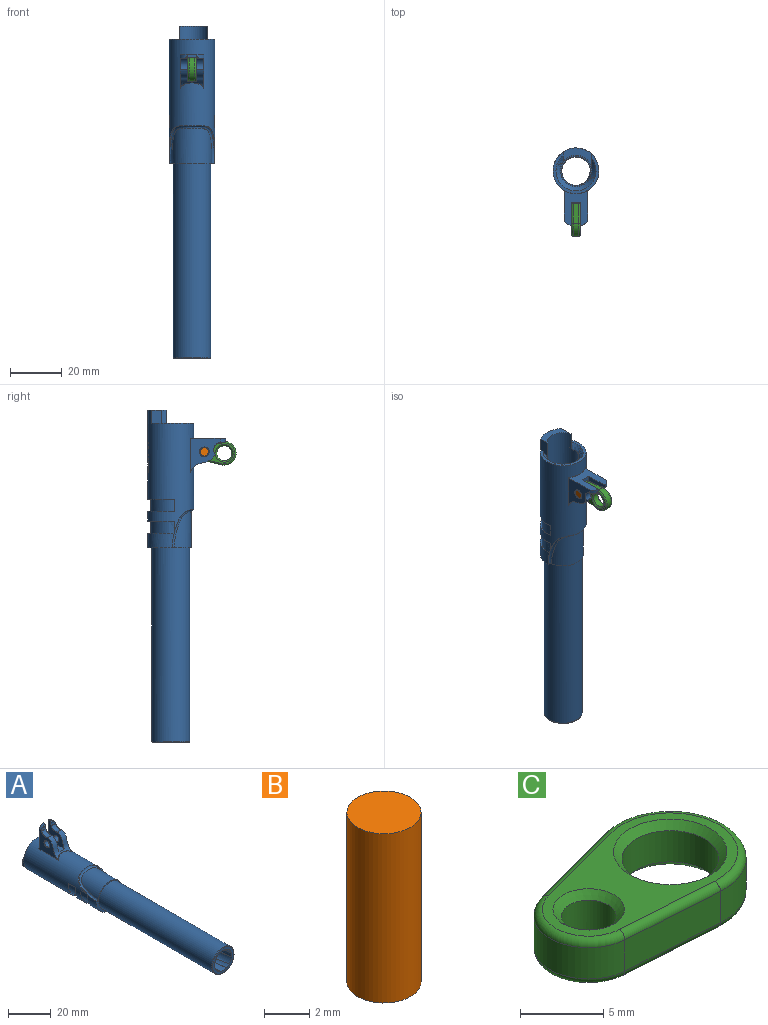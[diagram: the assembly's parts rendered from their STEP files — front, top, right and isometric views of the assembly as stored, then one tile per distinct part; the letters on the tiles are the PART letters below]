
ASSEMBLY  parts=3 mates=2
PART A: 333 faces, bbox 31.5x130.4x32.7 mm
  f0: bspline ~95.71x9.97mm, area 220mm2, adj f16,f17,f18,f23
  f1: bspline ~95.71x9.42mm, area 220mm2, adj f14,f15,f22,f23
  f2: bspline ~95.71x9.97mm, area 220mm2, adj f11,f12,f13,f23
  f3: bspline ~95.71x11mm, area 220mm2, adj f8,f9,f10,f23
  f4: bspline ~95.71x9.42mm, area 220mm2, adj f19,f20,f21,f23
  f5: bspline ~95.71x11mm, area 220mm2, adj f23,f24,f25,f26
  f6: bspline ~14.67x14.67mm, area 9.1mm2, adj f7,f23,f39
  f7: bspline ~14.67x14.67mm, area 9.1mm2, adj f6,f23,f39
  f8: bspline ~95.71x9.97mm, area 14.2mm2, adj f3,f9,f23,f42
  f9: plane 1.95x1.39mm, normal (0,-1,0), area 0.3mm2, adj f3,f8,f10,f42
  f10: bspline ~95.71x9.72mm, area 14.2mm2, adj f3,f9,f23,f42
  f11: bspline ~95.71x8mm, area 14.2mm2, adj f2,f12,f23,f42,f44
  f12: plane 2.28x0.36mm, normal (0,-1,0), area 0.3mm2, adj f2,f11,f13,f42
  f13: bspline ~95.71x9.71mm, area 14.2mm2, adj f2,f12,f23,f42,f43
  f14: bspline ~95.71x9.3mm, area 14.2mm2, adj f1,f15,f23,f42,f43
  f15: plane 2.1x1.12mm, normal (0,-1,0), area 0.3mm2, adj f1,f14,f22,f42
  f16: bspline ~95.71x8mm, area 14.2mm2, adj f0,f17,f23,f42
  f17: plane 2.28x0.36mm, normal (0,-1,0), area 0.3mm2, adj f0,f16,f18,f42
  f18: bspline ~95.71x9.71mm, area 14.2mm2, adj f0,f17,f23,f42
  f19: bspline ~95.71x9.3mm, area 14.2mm2, adj f4,f20,f23,f42
  f20: plane 2.1x1.12mm, normal (0,-1,0), area 0.3mm2, adj f4,f19,f21,f42
  f21: bspline ~95.71x7.31mm, area 14.2mm2, adj f4,f20,f23,f42
  f22: bspline ~95.71x7.31mm, area 14.2mm2, adj f1,f15,f23,f42
  f23: plane 14.17x14.17mm, normal (0,-1,0), area 53mm2, adj f0,f1,f2,f3,f4,f5,f6,f7
  f24: bspline ~95.71x9.97mm, area 14.2mm2, adj f5,f23,f25,f42
  f25: plane 1.95x1.39mm, normal (0,-1,0), area 0.3mm2, adj f5,f24,f26,f42
  f26: bspline ~95.71x9.72mm, area 14.2mm2, adj f5,f23,f25,f42
  f27: cylinder r=8.84mm len=1.49mm, axis (0,-1,0), area 1.3mm2, adj f45,f46,f47,f48,f49
  f28: cylinder r=8.84mm len=0.91mm, axis (0,-1,0), area 0.3mm2, adj f50,f51,f52,f53
  f29: cylinder r=8.84mm len=1.14mm, axis (0,-1,0), area 0.6mm2, adj f54,f55,f56,f57
  f30: cylinder r=8.84mm len=0.96mm, axis (0,-1,0), area 0.4mm2, adj f58,f59,f60,f61
  f31: cylinder r=8.84mm len=0.8mm, axis (0,-1,0), area 0.3mm2, adj f62,f63,f64
  f32: cylinder r=8.84mm len=0.8mm, axis (0,-1,0), area 0.3mm2, adj f65,f66,f67
  f33: cylinder r=8.84mm len=1.03mm, axis (0,-1,0), area 0.5mm2, adj f68,f69,f70,f71
  f34: cylinder r=1mm len=1.76mm, axis (-1,0,0), area 1.3mm2, adj f35,f76,f81
  f35: cylinder r=2.94mm len=2.85mm, axis (-1,0,0), area 3.9mm2, adj f34,f72,f76,f81,f260
  f36: cylinder r=2.94mm len=2.85mm, axis (-1,0,0), area 3.9mm2, adj f37,f74,f77,f79,f263
  f37: cylinder r=1mm len=1.76mm, axis (-1,0,0), area 1.3mm2, adj f36,f77,f79
  f38: bspline ~3.5x2.74mm, area 14.6mm2, adj f75,f79,f80,f81
  f39: cylinder r=7.32mm len=74.75mm, axis (0,1,0), area 3437.8mm2, adj f6,f7,f82
  f40: cylinder r=8.84mm len=1.06mm, axis (0,-1,0), area 0.4mm2, adj f83,f84,f85
  f41: cylinder r=8.84mm len=1.2mm, axis (0,-1,0), area 0.4mm2, adj f86,f87,f88
  f42: cylinder r=5.69mm len=97.7mm, axis (0,1,0), area 2001.4mm2, adj f8,f9,f10,f11,f12,f13,f14,f15
  f43: cylinder r=5.69mm len=65.84mm, axis (0,1,0), area 189mm2, adj f13,f14,f23,f42
  f44: cylinder r=5.69mm len=17.51mm, axis (0,1,0), area 18.9mm2, adj f11,f23,f42
  f45: bspline ~1.09x0.87mm, area 0.3mm2, adj f27,f46,f49,f90
  f46: bspline ~1.16x1mm, area 0.3mm2, adj f27,f45,f47,f90
  f47: bspline ~0.57x0.55mm, area 0.2mm2, adj f27,f46,f48,f90
  f48: bspline ~0.72x0.67mm, area 0.2mm2, adj f27,f47,f49,f90
  f49: bspline ~1.09x0.87mm, area 0.3mm2, adj f27,f45,f48,f90
  f50: bspline ~0.46x0.46mm, area 0.2mm2, adj f28,f51,f53,f91
  f51: bspline ~0.47x0.46mm, area 0.2mm2, adj f28,f50,f52,f91
  f52: bspline ~0.49x0.48mm, area 0.2mm2, adj f28,f51,f53,f91
  f53: bspline ~0.5x0.49mm, area 0.2mm2, adj f28,f50,f52,f91
  f54: bspline ~0.62x0.6mm, area 0.2mm2, adj f29,f55,f57,f91
  f55: bspline ~0.65x0.62mm, area 0.2mm2, adj f29,f54,f56,f91
  f56: bspline ~0.62x0.62mm, area 0.2mm2, adj f29,f55,f57,f91
  f57: bspline ~0.64x0.64mm, area 0.2mm2, adj f29,f54,f56,f91
  f58: bspline ~0.58x0.52mm, area 0.2mm2, adj f30,f59,f61,f98
  f59: bspline ~0.61x0.56mm, area 0.2mm2, adj f30,f58,f60,f98
  f60: bspline ~0.63x0.57mm, area 0.2mm2, adj f30,f59,f61,f98
  f61: bspline ~0.57x0.52mm, area 0.2mm2, adj f30,f58,f60,f98
  f62: plane 0.63x0.23mm, normal (0.9,0,0.44), area 0.2mm2, adj f31,f63,f64,f99
  f63: plane 0.92x0.46mm, normal (0,-1,0), area 0.2mm2, adj f31,f62,f64,f99
  f64: plane 0.92x0.64mm, normal (-0.55,0.79,-0.27), area 0.3mm2, adj f31,f62,f63,f99
  f65: plane 0.63x0.23mm, normal (0.9,0,0.44), area 0.2mm2, adj f32,f66,f67,f100
  f66: plane 0.92x0.46mm, normal (0,-1,0), area 0.2mm2, adj f32,f65,f67,f100
  f67: plane 0.92x0.64mm, normal (-0.55,0.79,-0.27), area 0.3mm2, adj f32,f65,f66,f100
  f68: bspline ~0.59x0.55mm, area 0.2mm2, adj f33,f69,f71,f101
  f69: bspline ~0.59x0.55mm, area 0.2mm2, adj f33,f68,f70,f101
  f70: bspline ~0.57x0.52mm, area 0.2mm2, adj f33,f69,f71,f101
  f71: bspline ~0.57x0.52mm, area 0.2mm2, adj f33,f68,f70,f101
  f72: cylinder r=1mm len=2.85mm, axis (-1,0,0), area 0.8mm2, adj f35,f81,f104,f260
  f73: cylinder r=1.68mm len=3.36mm, axis (1,0,0), area 28mm2, adj f81,f105,f106
  f74: cylinder r=1mm len=2.85mm, axis (-1,0,0), area 0.8mm2, adj f36,f79,f107,f263
  f75: plane 3.5x1.58mm, normal (0,0,1), area 5.5mm2, adj f38,f79,f81,f108
  f76: bspline ~2.85x2.12mm, area 4.6mm2, adj f34,f35,f81,f108,f260
  f77: bspline ~2.89x2.13mm, area 4.6mm2, adj f36,f37,f79,f108,f263
  f78: cylinder r=1.68mm len=3.36mm, axis (1,0,0), area 28mm2, adj f79,f109,f110
  f79: plane 11.85x10.66mm, normal (1,0,0), area 57.5mm2, adj f36,f37,f38,f74,f75,f77,f78,f80
  f80: plane 6.34x3.5mm, normal (0,0,1), area 22.2mm2, adj f38,f79,f81,f111
  f81: plane 11.85x10.66mm, normal (-1,0,0), area 57.5mm2, adj f34,f35,f38,f72,f73,f75,f76,f80
  f82: plane 17.7x16.69mm, normal (0,-1,0), area 51.9mm2, adj f39,f112,f113,f258,f266,f267
  f83: plane 1.22x0.5mm, normal (-0.38,-0.91,-0.18), area 0.3mm2, adj f40,f84,f85,f117
  f84: plane 1.22x0.5mm, normal (-0.38,0.9,-0.19), area 0.3mm2, adj f40,f83,f85,f117
  f85: plane 0.82x0.27mm, normal (0.9,0,0.44), area 0.2mm2, adj f40,f83,f84,f117
  f86: plane 0.68x0.27mm, normal (0.9,0,0.44), area 0.2mm2, adj f41,f87,f88,f119
  f87: plane 1.34x0.48mm, normal (0,-1,0), area 0.3mm2, adj f41,f86,f88,f119
  f88: plane 1.36x0.7mm, normal (-0.51,0.82,-0.25), area 0.4mm2, adj f41,f86,f87,f119
  f89: plane 12.12x12.12mm, normal (0,1,0), area 13.5mm2, adj f42,f120
  f90: cylinder r=8.58mm len=1.83mm, axis (0,-1,0), area 1.9mm2, adj f45,f46,f47,f48,f49,f124,f125,f126
  f91: cylinder r=8.58mm len=1.83mm, axis (0,-1,0), area 1.4mm2, adj f50,f51,f52,f53,f54,f55,f56,f57
  f92: cylinder r=8.58mm len=2.23mm, axis (0,-1,0), area 0.9mm2, adj f137,f138,f139,f140,f141,f142,f143
  f93: cylinder r=8.58mm len=2.23mm, axis (0,-1,0), area 0.9mm2, adj f144,f145,f146,f147,f148,f149,f150
  f94: cylinder r=8.58mm len=2.2mm, axis (0,-1,0), area 1.1mm2, adj f151,f152,f153,f154,f155,f156,f157,f158
  f95: cylinder r=8.58mm len=2.23mm, axis (0,-1,0), area 2.7mm2, adj f159,f160,f161,f162,f163,f164,f165,f166
  f96: cylinder r=8.58mm len=2.23mm, axis (0,-1,0), area 2.2mm2, adj f174,f175,f176,f177,f178,f179,f180,f181
  f97: cylinder r=8.58mm len=2.2mm, axis (0,-1,0), area 1.1mm2, adj f184,f185,f186,f187,f188,f189,f190,f191
  f98: cylinder r=8.58mm len=2.25mm, axis (0,-1,0), area 1.6mm2, adj f58,f59,f60,f61,f192,f193,f194,f195
  f99: cylinder r=8.58mm len=2.2mm, axis (0,-1,0), area 1.4mm2, adj f62,f63,f64,f202,f203,f204,f205,f206
  f100: cylinder r=8.58mm len=2.2mm, axis (0,-1,0), area 1.4mm2, adj f65,f66,f67,f213,f214,f215,f216,f217
  f101: cylinder r=8.58mm len=1.83mm, axis (0,-1,0), area 1.1mm2, adj f68,f69,f70,f71,f224,f225,f226,f227
  f102: cylinder r=8.58mm len=1.83mm, axis (0,-1,0), area 1.3mm2, adj f232,f233,f234,f235,f236,f237,f238,f239
  f103: plane 1.04x0.27mm, normal (-0.9,0,-0.44), area 0.3mm2, adj f117,f252,f253,f323
  f104: cylinder r=2.94mm len=4.3mm, axis (-1,0,0), area 14.6mm2, adj f72,f81,f111,f260
  f105: bspline ~3.76x3.76mm, area 1.7mm2, adj f73,f106,f260
  f106: bspline ~3.76x3.76mm, area 1.7mm2, adj f73,f105,f260
  f107: cylinder r=2.94mm len=4.3mm, axis (-1,0,0), area 14.6mm2, adj f74,f79,f111,f263
  f108: plane 13.52x9.24mm, normal (0,1,0), area 80.9mm2, adj f75,f76,f77,f79,f81,f260,f261,f262
  f109: bspline ~3.76x3.76mm, area 1.7mm2, adj f78,f110,f263
  f110: bspline ~3.76x3.76mm, area 1.7mm2, adj f78,f109,f263
  f111: bspline ~9.36x9.2mm, area 66mm2, adj f79,f80,f81,f104,f107,f259,f260,f263
  f112: cylinder r=7.82mm len=15.38mm, axis (0,-1,0), area 258.8mm2, adj f82,f266
  f113: cylinder r=8.84mm len=17.67mm, axis (0,-1,0), area 166.4mm2, adj f82,f114,f258,f267
  f114: plane 17.77x10.16mm, normal (0,1,0), area 19.9mm2, adj f113,f257,f258,f267,f268
  f115: cylinder r=8.58mm len=2.77mm, axis (0,-1,0), area 0.9mm2, adj f255,f273,f274,f275,f276,f277,f278,f279
  f116: cylinder r=8.58mm len=2.84mm, axis (0,-1,0), area 1.3mm2, adj f280,f281,f282,f283,f284,f285,f286,f287
  f117: cylinder r=8.58mm len=2.77mm, axis (0,-1,0), area 1.4mm2, adj f83,f84,f85,f103,f251,f252,f253,f254
  f118: cylinder r=8.58mm len=2.84mm, axis (0,-1,0), area 1.4mm2, adj f296,f297,f298,f299,f300,f301,f302,f303
  f119: cylinder r=8.58mm len=2.85mm, axis (0,-1,0), area 1.3mm2, adj f86,f87,f88,f250,f310,f311,f312,f313
  f120: cylinder r=6.06mm len=30.5mm, axis (0,1,0), area 987.5mm2, adj f89,f121,f122,f123,f249,f319,f320
  f121: bspline ~15.12x10.86mm, area 56.4mm2, adj f120,f122,f123,f321
  f122: bspline ~4.81x3.72mm, area 6.8mm2, adj f120,f121,f320,f321
  f123: bspline ~8.18x2.53mm, area 16.4mm2, adj f120,f121,f249,f321
  f124: bspline ~1.32x1.01mm, area 0.4mm2, adj f90,f125,f127,f323
  f125: bspline ~1.32x1.01mm, area 0.4mm2, adj f90,f124,f126,f323
  f126: bspline ~1.42x1.2mm, area 0.4mm2, adj f90,f125,f127,f323
  f127: bspline ~1.4x1.19mm, area 0.4mm2, adj f90,f124,f126,f323
  f128: bspline ~0.69x0.67mm, area 0.3mm2, adj f91,f129,f136,f323
  f129: bspline ~0.61x0.57mm, area 0.2mm2, adj f91,f128,f130,f323
  f130: bspline ~0.77x0.7mm, area 0.2mm2, adj f91,f129,f131,f323
  f131: bspline ~0.9x0.83mm, area 0.3mm2, adj f91,f130,f132,f323
  f132: bspline ~0.61x0.47mm, area 0.2mm2, adj f91,f131,f133,f323
  f133: bspline ~0.63x0.63mm, area 0.1mm2, adj f91,f132,f134,f323
  f134: bspline ~0.76x0.69mm, area 0.2mm2, adj f91,f133,f135,f323
  f135: bspline ~0.6x0.56mm, area 0.2mm2, adj f91,f134,f136,f323
  f136: bspline ~0.7x0.65mm, area 0.3mm2, adj f91,f128,f135,f323
  f137: bspline ~0.7x0.63mm, area 0.2mm2, adj f92,f138,f143,f323
  f138: plane 0.38x0.3mm, normal (0,-1,0), area 0.1mm2, adj f92,f137,f139,f323
  f139: bspline ~0.53x0.45mm, area 0.2mm2, adj f92,f138,f140,f323
  f140: plane 1.82x0.79mm, normal (0,-1,0), area 0.5mm2, adj f92,f139,f141,f323
  f141: plane 0.29x0.23mm, normal (-0.9,0,-0.44), area 0.1mm2, adj f92,f140,f142,f323
  f142: plane 2.34x0.89mm, normal (0,1,0), area 0.6mm2, adj f92,f141,f143,f323
  f143: plane 0.24x0.19mm, normal (0.9,0,0.44), area 0.1mm2, adj f92,f137,f142,f323
  f144: bspline ~0.7x0.63mm, area 0.2mm2, adj f93,f145,f150,f323
  f145: plane 0.38x0.3mm, normal (0,-1,0), area 0.1mm2, adj f93,f144,f146,f323
  f146: bspline ~0.53x0.45mm, area 0.2mm2, adj f93,f145,f147,f323
  f147: plane 1.82x0.79mm, normal (0,-1,0), area 0.5mm2, adj f93,f146,f148,f323
  f148: plane 0.29x0.23mm, normal (-0.9,0,-0.44), area 0.1mm2, adj f93,f147,f149,f323
  f149: plane 2.34x0.89mm, normal (0,1,0), area 0.6mm2, adj f93,f148,f150,f323
  f150: plane 0.24x0.19mm, normal (0.9,0,0.44), area 0.1mm2, adj f93,f144,f149,f323
  f151: plane 0.29x0.23mm, normal (-0.9,0,-0.44), area 0.1mm2, adj f94,f152,f158,f323
  f152: bspline ~0.69x0.54mm, area 0.2mm2, adj f94,f151,f153,f323
  f153: bspline ~1.49x1.09mm, area 0.4mm2, adj f94,f152,f154,f323
  f154: plane 0.36x0.28mm, normal (0,1,0), area 0.1mm2, adj f94,f153,f155,f323
  f155: plane 1.47x0.24mm, normal (0.9,0,0.44), area 0.4mm2, adj f94,f154,f156,f323
  f156: plane 0.42x0.29mm, normal (0,-1,0), area 0.1mm2, adj f94,f155,f157,f323
  f157: plane 1.17x0.24mm, normal (-0.9,0,-0.44), area 0.3mm2, adj f94,f156,f158,f323
  f158: bspline ~2.01x1.36mm, area 0.6mm2, adj f94,f151,f157,f323
  f159: plane 1.98x0.83mm, normal (-0.27,-0.95,-0.13), area 0.5mm2, adj f95,f160,f173,f323
  f160: plane 0.34x0.23mm, normal (-0.9,0,-0.44), area 0.1mm2, adj f95,f159,f161,f323
  f161: plane 1.98x0.83mm, normal (-0.27,0.95,-0.13), area 0.5mm2, adj f95,f160,f162,f323
  f162: plane 1.98x0.82mm, normal (0,-1,0), area 0.5mm2, adj f95,f161,f163,f323
  f163: plane 0.32x0.23mm, normal (-0.9,0,-0.44), area 0.1mm2, adj f95,f162,f164,f323
  f164: plane 2.34x0.89mm, normal (0,1,0), area 0.6mm2, adj f95,f163,f165,f323
  f165: plane 0.48x0.24mm, normal (0.9,0,0.44), area 0.1mm2, adj f95,f164,f166,f323
  f166: plane 1.69x0.63mm, normal (0.27,-0.95,0.13), area 0.4mm2, adj f95,f165,f167,f323
  f167: bspline ~0.46x0.42mm, area 0.1mm2, adj f95,f166,f168,f323
  f168: bspline ~0.43x0.41mm, area 0.1mm2, adj f95,f167,f169,f323
  f169: plane 1.71x0.64mm, normal (0.27,0.95,0.13), area 0.4mm2, adj f95,f168,f170,f323
  f170: plane 0.49x0.24mm, normal (0.9,0,0.44), area 0.1mm2, adj f95,f169,f171,f323
  f171: plane 2.34x0.89mm, normal (0,-1,0), area 0.6mm2, adj f95,f170,f172,f323
  f172: plane 0.32x0.23mm, normal (-0.9,0,-0.44), area 0.1mm2, adj f95,f171,f173,f323
  f173: plane 1.98x0.82mm, normal (0,1,0), area 0.5mm2, adj f95,f159,f172,f323
  f174: plane 1.75x1.1mm, normal (-0.49,-0.84,-0.24), area 0.5mm2, adj f96,f175,f183,f323
  f175: plane 0.34x0.23mm, normal (-0.9,0,-0.44), area 0.1mm2, adj f96,f174,f176,f323
  f176: plane 2.34x0.89mm, normal (0,1,0), area 0.6mm2, adj f96,f175,f177,f323
  f177: plane 0.32x0.24mm, normal (0.9,0,0.44), area 0.1mm2, adj f96,f176,f178,f323
  f178: plane 1.8x0.67mm, normal (0,-1,0), area 0.4mm2, adj f96,f177,f179,f323
  f179: plane 1.81x1.11mm, normal (0.49,0.84,0.24), area 0.5mm2, adj f96,f178,f180,f323
  f180: plane 0.34x0.24mm, normal (0.9,0,0.44), area 0.1mm2, adj f96,f179,f181,f323
  f181: plane 2.34x0.89mm, normal (0,-1,0), area 0.6mm2, adj f96,f180,f182,f323
  f182: plane 0.32x0.23mm, normal (-0.9,0,-0.44), area 0.1mm2, adj f96,f181,f183,f323
  f183: plane 1.75x0.77mm, normal (0,1,0), area 0.4mm2, adj f96,f174,f182,f323
  f184: plane 0.29x0.23mm, normal (-0.9,0,-0.44), area 0.1mm2, adj f97,f185,f191,f323
  f185: bspline ~0.69x0.54mm, area 0.2mm2, adj f97,f184,f186,f323
  f186: bspline ~1.49x1.09mm, area 0.4mm2, adj f97,f185,f187,f323
  f187: plane 0.36x0.28mm, normal (0,1,0), area 0.1mm2, adj f97,f186,f188,f323
  f188: plane 1.47x0.24mm, normal (0.9,0,0.44), area 0.4mm2, adj f97,f187,f189,f323
  f189: plane 0.42x0.29mm, normal (0,-1,0), area 0.1mm2, adj f97,f188,f190,f323
  f190: plane 1.17x0.24mm, normal (-0.9,0,-0.44), area 0.3mm2, adj f97,f189,f191,f323
  f191: bspline ~2.01x1.36mm, area 0.6mm2, adj f97,f184,f190,f323
  f192: bspline ~1.22x0.96mm, area 0.4mm2, adj f98,f193,f201,f323
  f193: bspline ~0.88x0.75mm, area 0.3mm2, adj f98,f192,f194,f323
  f194: bspline ~0.84x0.68mm, area 0.3mm2, adj f98,f193,f195,f323
  f195: bspline ~0.53x0.4mm, area 0.2mm2, adj f98,f194,f196,f323
  f196: bspline ~0.27x0.17mm, area 0mm2, adj f98,f195,f197,f323
  f197: bspline ~0.88x0.67mm, area 0.3mm2, adj f98,f196,f198,f323
  f198: bspline ~0.45x0.41mm, area 0.1mm2, adj f98,f197,f199,f323
  f199: plane 0.3x0.25mm, normal (0.89,-0.1,0.44), area 0.1mm2, adj f98,f198,f200,f323
  f200: bspline ~0.66x0.63mm, area 0.2mm2, adj f98,f199,f201,f323
  f201: bspline ~1.26x0.88mm, area 0.4mm2, adj f98,f192,f200,f323
  f202: plane 0.29x0.23mm, normal (-0.9,0,-0.44), area 0.1mm2, adj f99,f203,f212,f323
  f203: plane 0.39x0.33mm, normal (0,1,0), area 0.1mm2, adj f99,f202,f204,f323
  f204: plane 0.29x0.23mm, normal (0.9,0,0.44), area 0.1mm2, adj f99,f203,f205,f323
  f205: plane 1.51x0.58mm, normal (0,1,0), area 0.4mm2, adj f99,f204,f206,f323
  f206: plane 0.24x0.21mm, normal (0.9,0,0.44), area 0.1mm2, adj f99,f205,f207,f323
  f207: plane 1.52x1.09mm, normal (0.55,-0.79,0.27), area 0.5mm2, adj f99,f206,f208,f323
  f208: plane 0.39x0.33mm, normal (0,-1,0), area 0.1mm2, adj f99,f207,f209,f323
  f209: plane 1x0.23mm, normal (-0.9,0,-0.44), area 0.3mm2, adj f99,f208,f210,f323
  f210: plane 0.63x0.44mm, normal (0,-1,0), area 0.1mm2, adj f99,f209,f211,f323
  f211: plane 0.29x0.23mm, normal (-0.9,0,-0.44), area 0.1mm2, adj f99,f210,f212,f323
  f212: plane 0.63x0.44mm, normal (0,1,0), area 0.1mm2, adj f99,f202,f211,f323
  f213: plane 0.29x0.23mm, normal (-0.9,0,-0.44), area 0.1mm2, adj f100,f214,f223,f323
  f214: plane 0.39x0.33mm, normal (0,1,0), area 0.1mm2, adj f100,f213,f215,f323
  f215: plane 0.29x0.23mm, normal (0.9,0,0.44), area 0.1mm2, adj f100,f214,f216,f323
  f216: plane 1.51x0.58mm, normal (0,1,0), area 0.4mm2, adj f100,f215,f217,f323
  f217: plane 0.24x0.21mm, normal (0.9,0,0.44), area 0.1mm2, adj f100,f216,f218,f323
  f218: plane 1.52x1.09mm, normal (0.55,-0.79,0.27), area 0.5mm2, adj f100,f217,f219,f323
  f219: plane 0.39x0.33mm, normal (0,-1,0), area 0.1mm2, adj f100,f218,f220,f323
  f220: plane 1x0.23mm, normal (-0.9,0,-0.44), area 0.3mm2, adj f100,f219,f221,f323
  f221: plane 0.63x0.44mm, normal (0,-1,0), area 0.1mm2, adj f100,f220,f222,f323
  f222: plane 0.29x0.23mm, normal (-0.9,0,-0.44), area 0.1mm2, adj f100,f221,f223,f323
  f223: plane 0.63x0.44mm, normal (0,1,0), area 0.1mm2, adj f100,f213,f222,f323
  f224: bspline ~0.81x0.71mm, area 0.3mm2, adj f101,f225,f231,f323
  f225: bspline ~0.8x0.73mm, area 0.3mm2, adj f101,f224,f226,f323
  f226: bspline ~0.82x0.71mm, area 0.3mm2, adj f101,f225,f227,f323
  f227: bspline ~0.26x0.24mm, area 0.1mm2, adj f101,f226,f228,f323
  f228: plane 0.98x0.8mm, normal (0.51,-0.83,0.25), area 0.3mm2, adj f101,f227,f229,f323
  f229: plane 0.35x0.2mm, normal (-0.74,-0.57,-0.36), area 0.1mm2, adj f101,f228,f230,f323
  f230: plane 1.08x0.88mm, normal (-0.51,0.83,-0.25), area 0.3mm2, adj f101,f229,f231,f323
  f231: bspline ~0.81x0.71mm, area 0.2mm2, adj f101,f224,f230,f323
  f232: bspline ~0.59x0.49mm, area 0.2mm2, adj f102,f233,f248,f323
  f233: plane 0.4x0.3mm, normal (0,-1,0), area 0.1mm2, adj f102,f232,f234,f323
  f234: bspline ~0.7x0.63mm, area 0.3mm2, adj f102,f233,f235,f323
  f235: bspline ~0.65x0.64mm, area 0.2mm2, adj f102,f234,f236,f323
  f236: bspline ~0.39x0.35mm, area 0.1mm2, adj f102,f235,f237,f323
  f237: bspline ~0.5x0.46mm, area 0.1mm2, adj f102,f236,f238,f323
  f238: plane 0.24x0.21mm, normal (0.9,0,0.44), area 0.1mm2, adj f102,f237,f239,f323
  f239: bspline ~0.85x0.8mm, area 0.3mm2, adj f102,f238,f240,f323
  f240: bspline ~0.92x0.85mm, area 0.3mm2, adj f102,f239,f241,f323
  f241: bspline ~0.55x0.55mm, area 0.1mm2, adj f102,f240,f242,f323
  f242: bspline ~0.38x0.32mm, area 0.1mm2, adj f102,f241,f243,f323
  f243: bspline ~0.59x0.55mm, area 0.1mm2, adj f102,f242,f244,f323
  f244: bspline ~0.71x0.67mm, area 0.3mm2, adj f102,f243,f245,f323
  f245: bspline ~0.69x0.68mm, area 0.3mm2, adj f102,f244,f246,f323
  f246: plane 0.23x0.21mm, normal (-0.9,0,-0.44), area 0.1mm2, adj f102,f245,f247,f323
  f247: bspline ~0.48x0.46mm, area 0.2mm2, adj f102,f246,f248,f323
  f248: bspline ~0.47x0.46mm, area 0.2mm2, adj f102,f232,f247,f323
  f249: plane 7.53x5.48mm, normal (1,0,0), area 29.6mm2, adj f120,f123,f319,f321,f323
  f250: plane 0.25x0.21mm, normal (-0.9,0,-0.44), area 0.1mm2, adj f119,f310,f318,f323
  f251: plane 0.25x0.22mm, normal (-0.9,0,-0.44), area 0.1mm2, adj f117,f252,f295,f323
  f252: plane 0.96x0.35mm, normal (-0.39,0.9,-0.19), area 0.2mm2, adj f103,f117,f251,f323
  f253: plane 0.96x0.34mm, normal (-0.38,-0.91,-0.18), area 0.2mm2, adj f103,f117,f254,f323
  f254: plane 0.25x0.22mm, normal (-0.9,0,-0.44), area 0.1mm2, adj f117,f253,f293,f323
  f255: plane 0.25x0.21mm, normal (-0.9,0,-0.44), area 0.1mm2, adj f115,f273,f279,f323
  f256: bspline ~9.43x9.35mm, area 66.6mm2, adj f270,f271,f272,f323
  f257: bspline ~9.43x9.35mm, area 66.4mm2, adj f114,f258,f268,f269,f323
  f258: bspline ~14.78x7.94mm, area 5.4mm2, adj f82,f113,f114,f257,f266,f323
  f259: cylinder r=1mm len=0.62mm, axis (-1,0,0), area 0.1mm2, adj f111,f260,f265,f323
  f260: plane 13.18x11.5mm, normal (1,0,0), area 81.1mm2, adj f35,f72,f76,f104,f105,f106,f108,f111
  f261: bspline ~4.68x1.41mm, area 0.8mm2, adj f108,f260,f262,f323
  f262: bspline ~4.68x1.41mm, area 0.8mm2, adj f108,f261,f263,f323
  f263: plane 13.18x11.5mm, normal (-1,0,0), area 81.1mm2, adj f36,f74,f77,f107,f108,f109,f110,f111
  f264: cylinder r=1mm len=0.62mm, axis (-1,0,0), area 0.1mm2, adj f111,f263,f265,f323
  f265: bspline ~8.83x1.69mm, area 0.7mm2, adj f111,f259,f264,f323
  f266: bspline ~17.36x14.71mm, area 59mm2, adj f82,f112,f258,f267,f323
  f267: bspline ~14.78x7.94mm, area 5.4mm2, adj f82,f113,f114,f266,f268,f323
  f268: bspline ~9.43x9.35mm, area 66.4mm2, adj f114,f257,f267,f269,f323
  f269: plane 17.81x10.57mm, normal (0,-1,0), area 19.9mm2, adj f257,f268,f323
  f270: plane 17.81x10.57mm, normal (0,1,0), area 19.9mm2, adj f256,f271,f323
  f271: bspline ~9.43x9.35mm, area 66.6mm2, adj f256,f270,f272,f323
  f272: plane 17.81x10.57mm, normal (0,-1,0), area 19.9mm2, adj f256,f271,f323
  f273: plane 2.59x0.62mm, normal (0,1,0), area 0.6mm2, adj f115,f255,f274,f323
  f274: plane 0.5x0.31mm, normal (-0.9,0,-0.44), area 0.2mm2, adj f115,f273,f275,f323
  f275: plane 0.46x0.41mm, normal (0,1,0), area 0.1mm2, adj f115,f274,f276,f323
  f276: plane 1.2x0.32mm, normal (0.9,0,0.44), area 0.4mm2, adj f115,f275,f277,f323
  f277: plane 0.46x0.41mm, normal (0,-1,0), area 0.1mm2, adj f115,f276,f278,f323
  f278: plane 0.5x0.31mm, normal (-0.9,0,-0.44), area 0.2mm2, adj f115,f277,f279,f323
  f279: plane 2.59x0.62mm, normal (0,-1,0), area 0.6mm2, adj f115,f255,f278,f323
  f280: bspline ~1.23x1.17mm, area 0.4mm2, adj f116,f281,f292,f323
  f281: plane 1.86x0.67mm, normal (0,1,0), area 0.4mm2, adj f116,f280,f282,f323
  f282: plane 0.32x0.21mm, normal (0.9,0,0.44), area 0.1mm2, adj f116,f281,f283,f323
  f283: plane 1.85x0.67mm, normal (0,-1,0), area 0.4mm2, adj f116,f282,f284,f323
  f284: bspline ~0.62x0.55mm, area 0.1mm2, adj f116,f283,f285,f323
  f285: bspline ~0.63x0.57mm, area 0.2mm2, adj f116,f284,f286,f323
  f286: bspline ~0.67x0.63mm, area 0.2mm2, adj f116,f285,f287,f323
  f287: bspline ~0.58x0.49mm, area 0.1mm2, adj f116,f286,f288,f323
  f288: plane 1.86x0.68mm, normal (0,1,0), area 0.4mm2, adj f116,f287,f289,f323
  f289: plane 0.32x0.21mm, normal (0.9,0,0.44), area 0.1mm2, adj f116,f288,f290,f323
  f290: plane 1.87x0.68mm, normal (0,-1,0), area 0.4mm2, adj f116,f289,f291,f323
  f291: bspline ~0.74x0.7mm, area 0.1mm2, adj f116,f290,f292,f323
  f292: bspline ~0.72x0.7mm, area 0.3mm2, adj f116,f280,f291,f323
  f293: plane 2.89x1.06mm, normal (0.38,0.91,0.18), area 0.8mm2, adj f117,f254,f294,f323
  f294: plane 0.32x0.16mm, normal (0.9,0,0.44), area 0mm2, adj f117,f293,f295,f323
  f295: plane 2.89x1.08mm, normal (0.39,-0.9,0.19), area 0.8mm2, adj f117,f251,f294,f323
  f296: bspline ~1.05x1.01mm, area 0.4mm2, adj f118,f297,f309,f323
  f297: bspline ~1.07x1.04mm, area 0.4mm2, adj f118,f296,f298,f323
  f298: bspline ~0.34x0.27mm, area 0.1mm2, adj f118,f297,f299,f323
  f299: plane 0.91x0.48mm, normal (-0.18,0.98,-0.09), area 0.2mm2, adj f118,f298,f300,f323
  f300: plane 0.78x0.31mm, normal (-0.9,0,-0.44), area 0.3mm2, adj f118,f299,f301,f323
  f301: plane 0.46x0.41mm, normal (0,1,0), area 0.1mm2, adj f118,f300,f302,f323
  f302: plane 0.94x0.32mm, normal (0.9,0,0.44), area 0.3mm2, adj f118,f301,f303,f323
  f303: plane 1.59x0.65mm, normal (0.18,-0.98,0.09), area 0.4mm2, adj f118,f302,f304,f323
  f304: bspline ~0.51x0.41mm, area 0.2mm2, adj f118,f303,f305,f323
  f305: bspline ~0.8x0.73mm, area 0.3mm2, adj f118,f304,f306,f323
  f306: bspline ~0.81x0.8mm, area 0.3mm2, adj f118,f305,f307,f323
  f307: bspline ~0.65x0.6mm, area 0.2mm2, adj f118,f306,f308,f323
  f308: plane 0.26x0.21mm, normal (0.9,0,0.44), area 0.1mm2, adj f118,f307,f309,f323
  f309: bspline ~0.86x0.85mm, area 0.3mm2, adj f118,f296,f308,f323
  f310: plane 0.72x0.28mm, normal (0,1,0), area 0.2mm2, adj f119,f250,f311,f323
  f311: plane 0.26x0.26mm, normal (-0.9,0,-0.44), area 0.1mm2, adj f119,f310,f312,f323
  f312: plane 0.4x0.29mm, normal (0,1,0), area 0.1mm2, adj f119,f311,f313,f323
  f313: plane 0.27x0.26mm, normal (0.9,0,0.44), area 0.1mm2, adj f119,f312,f314,f323
  f314: plane 2.11x0.72mm, normal (0,1,0), area 0.5mm2, adj f119,f313,f315,f323
  f315: plane 0.32x0.16mm, normal (0.9,0,0.44), area 0mm2, adj f119,f314,f316,f323
  f316: plane 2.38x1.25mm, normal (0.51,-0.82,0.25), area 0.7mm2, adj f119,f315,f317,f323
  f317: plane 1.08x0.26mm, normal (-0.9,0,-0.44), area 0.3mm2, adj f119,f316,f318,f323
  f318: plane 0.72x0.28mm, normal (0,-1,0), area 0.2mm2, adj f119,f250,f317,f323
  f319: plane 10.72x7.27mm, normal (0,1,0), area 33.8mm2, adj f120,f249,f320,f323
  f320: plane 7.1x3.76mm, normal (-1,0,0), area 21.6mm2, adj f120,f122,f319,f321,f323
  f321: plane 19.87x18.41mm, normal (0,1,0), area 44.5mm2, adj f121,f122,f123,f249,f320,f323
  f322: cylinder r=8.84mm len=2.32mm, axis (0,-1,0), area 2.3mm2, adj f324,f325,f326,f327
  f323: cylinder r=8.84mm len=46.21mm, axis (0,-1,0), area 1788.2mm2, adj f103,f124,f125,f126,f127,f128,f129,f130
  f324: bspline ~1.41x1.35mm, area 0.5mm2, adj f322,f325,f327,f332
  f325: bspline ~1.43x1.37mm, area 0.5mm2, adj f322,f324,f326,f332
  f326: bspline ~1.25x1.21mm, area 0.5mm2, adj f322,f325,f327,f332
  f327: bspline ~1.25x1.21mm, area 0.5mm2, adj f322,f324,f326,f332
  f328: bspline ~1.74x1.68mm, area 0.5mm2, adj f323,f329,f331,f332
  f329: bspline ~1.74x1.68mm, area 0.5mm2, adj f323,f328,f330,f332
  f330: bspline ~1.52x1.42mm, area 0.6mm2, adj f323,f329,f331,f332
  f331: bspline ~1.5x1.41mm, area 0.5mm2, adj f323,f328,f330,f332
  f332: cylinder r=8.58mm len=2.92mm, axis (0,-1,0), area 1.2mm2, adj f324,f325,f326,f327,f328,f329,f330,f331
PART B: 3 faces, bbox 3.3x3.3x9.2 mm
  f0: plane 3.29x3.29mm, normal (0,0,-1), area 8.5mm2, adj f2
  f1: plane 3.29x3.29mm, normal (0,0,1), area 8.5mm2, adj f2
  f2: cylinder r=1.65mm len=9.2mm, axis (0,0,-1), area 95.1mm2, adj f0,f1
PART C: 20 faces, bbox 16.2x9.8x3.3 mm
  f0: plane 7.63x2.3mm, normal (-0.06,-1,0), area 17.6mm2, adj f1,f2,f8,f12
  f1: cylinder r=4.55mm len=9.1mm, axis (0,0,-1), area 36.3mm2, adj f0,f4,f9,f13
  f2: cylinder r=3.29mm len=6.46mm, axis (0,0,-1), area 21.3mm2, adj f0,f4,f10,f14
  f3: cylinder r=2.91mm len=5.82mm, axis (0,0,-1), area 42.1mm2, adj f17,f18
  f4: plane 7.37x2.3mm, normal (-0.26,0.97,0), area 17.6mm2, adj f1,f2,f11,f15
  f5: cylinder r=1.65mm len=3.3mm, axis (0,0,-1), area 23.8mm2, adj f16,f19
  f6: plane 14.54x8.1mm, normal (0,0,-1), area 40.6mm2, adj f12,f13,f14,f15,f16,f17
  f7: plane 14.54x8.1mm, normal (0,0,1), area 40.6mm2, adj f8,f9,f10,f11,f18,f19
  f8: cylinder r=0.5mm len=7.66mm, axis (-1,0.06,0), area 6mm2, adj f0,f7,f9,f10
  f9: torus R=4.05mm, axis (0,0,1), area 11.9mm2, adj f1,f7,f8,f11
  f10: torus R=2.79mm, axis (0,0,1), area 6.9mm2, adj f2,f7,f8,f11
  f11: cylinder r=0.5mm len=7.5mm, axis (-0.97,-0.26,0), area 6mm2, adj f4,f7,f9,f10
  f12: cylinder r=0.5mm len=7.66mm, axis (1,-0.06,0), area 6mm2, adj f0,f6,f13,f14
  f13: torus R=4.05mm, axis (0,0,1), area 11.9mm2, adj f1,f6,f12,f15
  f14: torus R=2.79mm, axis (0,0,1), area 6.9mm2, adj f2,f6,f12,f15
  f15: cylinder r=0.5mm len=7.5mm, axis (0.97,0.26,0), area 6mm2, adj f4,f6,f13,f14
  f16: cone r=1.65mm half-angle=45deg, axis (0,0,-1), area 8.4mm2, adj f5,f6
  f17: cone r=2.91mm half-angle=45deg, axis (0,0,-1), area 14mm2, adj f3,f6
  f18: cone r=2.91mm half-angle=45deg, axis (0,0,1), area 14mm2, adj f3,f7
  f19: cone r=2.15mm half-angle=45deg, axis (0,0,1), area 8.4mm2, adj f5,f7
PLACE A rot(axis=(1,0,0),90deg) t=(0,0,-156.6)mm fixed
PLACE B rot(axis=(0,1,0),90deg) t=(-4.6,-12.92,-16.16)mm
PLACE C rot(axis=(-0.58,0.57,-0.58),120.9deg) t=(-1.65,-19.91,-21.28)mm
MATE fastened B.f2 <-> A.f78  axis (-1,0,0) through (-4.6,-12.92,-16.16)mm
MATE revolute C.f16 <-> B.f2  axis (-1,0,0) through (0,-12.92,-16.16)mm
